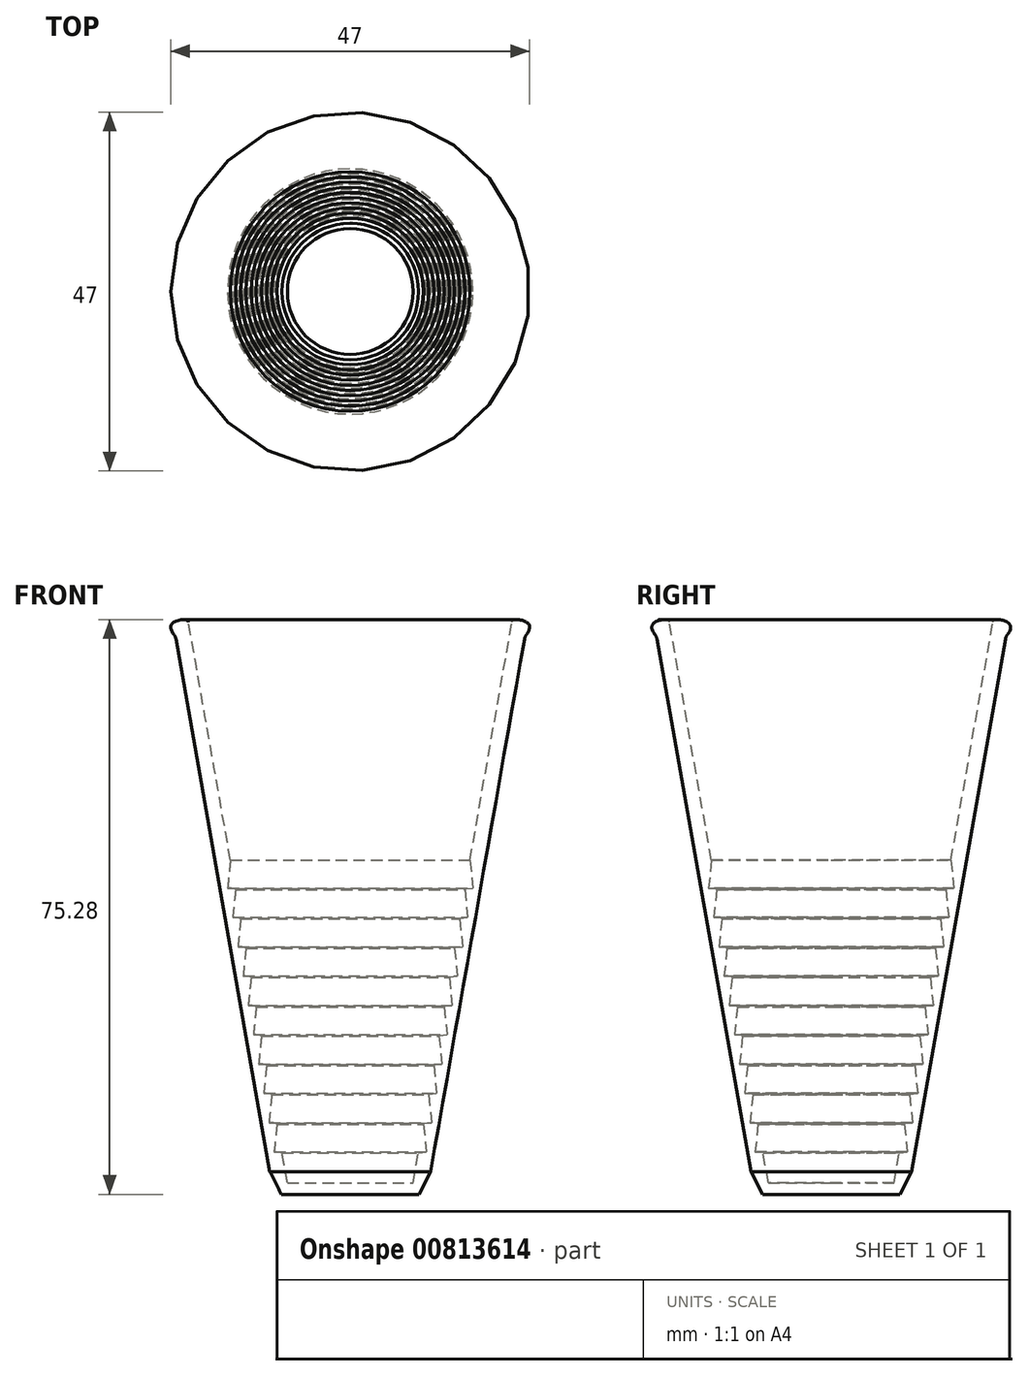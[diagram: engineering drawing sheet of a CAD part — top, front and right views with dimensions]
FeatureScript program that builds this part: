
annotation { "Feature Type Name" : "Feature", "Feature Type Description" : "" }
export const myFeature = defineFeature(function(context is Context, id is Id, definition is map)
    precondition{}
    {
        {
            var Q0;
            Q0=qCreatedBy(makeId("Front.planeOp"),FACE);
            var sketch = newSketch(context, id + "F0", { "sketchPlane" : qUnion([Q0])});
            skLineSegment(sketch, "E0", {"start": v(0, 0) * mm, "end": v(10, 0) * mm});
            skLineSegment(sketch, "E1", {"start": v(10, 0) * mm, "end": v(22.9, 73.13) * mm});
            skFitSpline(sketch, "E2", {"points": [v(22.9, 73.13) * mm, v(23.23, 74.86) * mm, v(21.2, 75) * mm], "startDerivative": vector(3.6, 3.7) * mm, "endDerivative": vector(-0.47, -2.64) * mm});
            skLineSegment(sketch, "E3", {"start": v(0, 0) * mm, "end": v(0, 1.5) * mm});
            skLineSegment(sketch, "E4", {"start": v(0, 1.5) * mm, "end": v(8.23, 1.5) * mm});
            skLineSegment(sketch, "E5", {"start": v(8.23, 1.5) * mm, "end": v(21.2, 75) * mm});
            skLineSegment(sketch, "E6", {"start": v(21.2, 75) * mm, "end": v(21.2, 75) * mm});
            skLineSegment(sketch, "E7", {"start": v(9.6, 9.21) * mm, "end": v(9.97, 5.56) * mm});
            skLineSegment(sketch, "E8", {"start": v(9.97, 5.56) * mm, "end": v(8.93, 5.46) * mm});
            skLineSegment(sketch, "E9.0.1.0", {"start": v(10.64, 9.4) * mm, "end": v(9.6, 9.3) * mm});
            skLineSegment(sketch, "E9.0.1.1", {"start": v(10.27, 13.05) * mm, "end": v(10.64, 9.4) * mm});
            skLineSegment(sketch, "E9.0.2.0", {"start": v(11.32, 13.24) * mm, "end": v(10.29, 13.14) * mm});
            skLineSegment(sketch, "E9.0.2.1", {"start": v(10.95, 16.9) * mm, "end": v(11.32, 13.24) * mm});
            skLineSegment(sketch, "E9.0.3.0", {"start": v(12, 17.09) * mm, "end": v(10.96, 16.98) * mm});
            skLineSegment(sketch, "E9.0.3.1", {"start": v(11.63, 20.74) * mm, "end": v(12, 17.09) * mm});
            skLineSegment(sketch, "E9.0.4.0", {"start": v(12.67, 20.93) * mm, "end": v(11.64, 20.82) * mm});
            skLineSegment(sketch, "E9.0.4.1", {"start": v(12.3, 24.58) * mm, "end": v(12.67, 20.93) * mm});
            skLineSegment(sketch, "E9.0.5.0", {"start": v(13.35, 24.77) * mm, "end": v(12.32, 24.66) * mm});
            skLineSegment(sketch, "E9.0.5.1", {"start": v(12.98, 28.42) * mm, "end": v(13.35, 24.77) * mm});
            skLineSegment(sketch, "E9.0.6.0", {"start": v(14.03, 28.6) * mm, "end": v(13, 28.5) * mm});
            skLineSegment(sketch, "E9.0.6.1", {"start": v(13.66, 32.26) * mm, "end": v(14.03, 28.6) * mm});
            skLineSegment(sketch, "E9.0.7.0", {"start": v(14.7, 32.45) * mm, "end": v(13.67, 32.34) * mm});
            skLineSegment(sketch, "E9.0.7.1", {"start": v(14.33, 36.1) * mm, "end": v(14.7, 32.45) * mm});
            skLineSegment(sketch, "E9.0.8.0", {"start": v(15.38, 36.29) * mm, "end": v(14.35, 36.18) * mm});
            skLineSegment(sketch, "E9.0.8.1", {"start": v(15.01, 39.94) * mm, "end": v(15.38, 36.29) * mm});
            skLineSegment(sketch, "E9.0.9.0", {"start": v(16.06, 40.13) * mm, "end": v(15.03, 40.02) * mm});
            skLineSegment(sketch, "E9.0.9.1", {"start": v(15.69, 43.78) * mm, "end": v(16.06, 40.13) * mm});
            skLineSegment(sketch, "E9.direction1", {"start": v(8.93, 5.46) * mm, "end": v(33.93, 5.46) * mm, "construction": true});
            skLineSegment(sketch, "E9.direction2", {"start": v(8.93, 5.46) * mm, "end": v(9.6, 9.3) * mm, "construction": true});
            skSolve(sketch);
        }
        {
            var Q0;
            Q0=makeQuery(id+"F0.imprint","IMPRINT",FACE,{"disambiguationData":[TD([[makeQuery(id+"F0.imprint","IMPRINT",EDGE,{"derivedFrom":sQuery(id+"F0.wireOp",EDGE,"E0")}),1.0]])]});
            var Q1;
            Q1=sQuery(id+"F0.wireOp",EDGE,"E3");
            revolve(context, id + "F1", {"surfaceOperationType" : NewSurfaceOperationType.NEW, "entities" : qUnion([Q0]), "axis" : qUnion([Q1]), "revolveType" : RevolveType.FULL});
        }
        {
            var Q0;
            Q0=makeQuery(id+"F1.opRevolve","SWEPT_EDGE",EDGE,{"disambiguationData":[OSD([sQuery(id+"F0.wireOp",EDGE,"E1"),sQuery(id+"F0.wireOp",EDGE,"E2")])]});
            fillet(context, id + "F2", {"entities" : qUnion([Q0]), "radius" : 1.5 * mm, "tangentPropagation" : true, "allowEdgeOverflow" : false});
        }
        {
            var Q0;
            Q0=makeQuery(id+"F1.opRevolve","SWEPT_EDGE",EDGE,{"disambiguationData":[OSD([sQuery(id+"F0.wireOp",EDGE,"E0"),sQuery(id+"F0.wireOp",EDGE,"E1")])]});
            chamfer(context, id + "F3", {"entities" : qUnion([Q0]), "chamferType" : ChamferType.TWO_OFFSETS, "width1" : 1 * mm, "oppositeDirection" : false, "width2" : 3 * mm, "tangentPropagation" : true});
        }
    });
